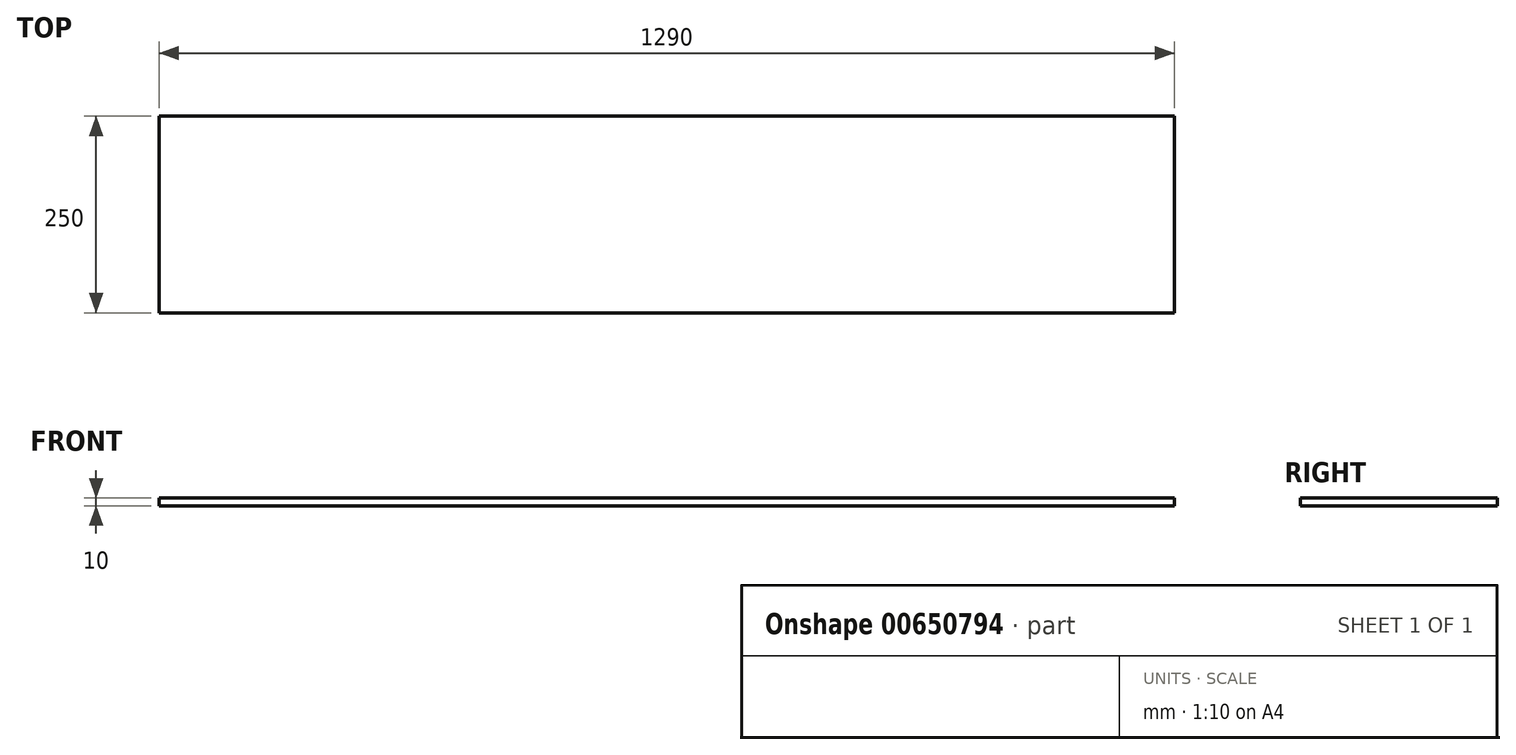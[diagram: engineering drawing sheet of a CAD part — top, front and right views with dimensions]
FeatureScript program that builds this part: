
annotation { "Feature Type Name" : "Feature", "Feature Type Description" : "" }
export const myFeature = defineFeature(function(context is Context, id is Id, definition is map)
    precondition{}
    {
        {
            var Q0;
            Q0=qCreatedBy(makeId("Top.planeOp"),FACE);
            var sketch = newSketch(context, id + "F0", { "sketchPlane" : qUnion([Q0])});
            skLineSegment(sketch, "E0.bottom", {"start": v(-2067.28, 0) * mm, "end": v(-777.28, 0) * mm});
            skLineSegment(sketch, "E0.top", {"start": v(-2067.28, -250) * mm, "end": v(-777.28, -250) * mm});
            skLineSegment(sketch, "E0.left", {"start": v(-2067.28, 0) * mm, "end": v(-2067.28, -250) * mm});
            skLineSegment(sketch, "E0.right", {"start": v(-777.28, 0) * mm, "end": v(-777.28, -250) * mm});
            skSolve(sketch);
        }
        {
            var Q0;
            Q0=makeQuery(id+"F0.imprint","IMPRINT",FACE,{"disambiguationData":[TD([[makeQuery(id+"F0.imprint","IMPRINT",EDGE,{"derivedFrom":sQuery(id+"F0.wireOp",EDGE,"E0.bottom")}),-1.0]])]});
            extrude(context, id + "F1", {"entities" : qUnion([Q0]), "depth" : 10 * mm, "offsetDistance" : 25 * mm});
        }
    });
